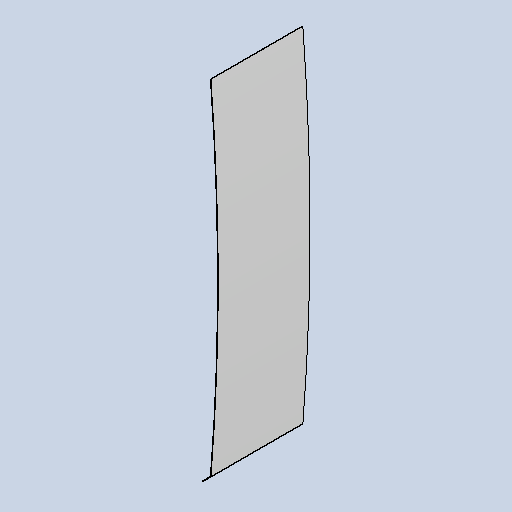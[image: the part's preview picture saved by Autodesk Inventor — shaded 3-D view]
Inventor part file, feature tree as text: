
AUTODESK INVENTOR PART (.ipt)
format: ipt  version: 2025 (Build 290162010, 162A)  size: 318,976 bytes
history: native  units: mm
features: other x4, sheet_metal_op x3, sketch x2
ambient origin geometry x8: Origin, YZ Plane, XZ Plane, XY Plane, X Axis, Y Axis, Z Axis, Center Point
bodies: Body1 (feature_tree)
feature tree (9):
  sheet_metal_op  "Contour Flange2"
  other  "Mark3"
  other  "A-Side Definition"
  sketch  "Sketch1"  dims[d36=3.0mm]
  other  "Plate2"
  sheet_metal_op  "Bend2"
  sheet_metal_op  "Corner2"
  sketch  "Sketch4"  dims[d37=3.0mm d38=1.5mm d39=6.0mm d40=5.0mm d41=492.0mm d42=5.0mm d43=3.0mm d44=12.0mm d45=3.0mm d46=5.0mm d65=8.0mm d78=3.0mm d80=3.0mm d148=5.0mm d153=63.0mm d165=11050.0mm d167=23.736478mm d169=1843.0mm d170=0.0mm]
  other  "Definition1"
